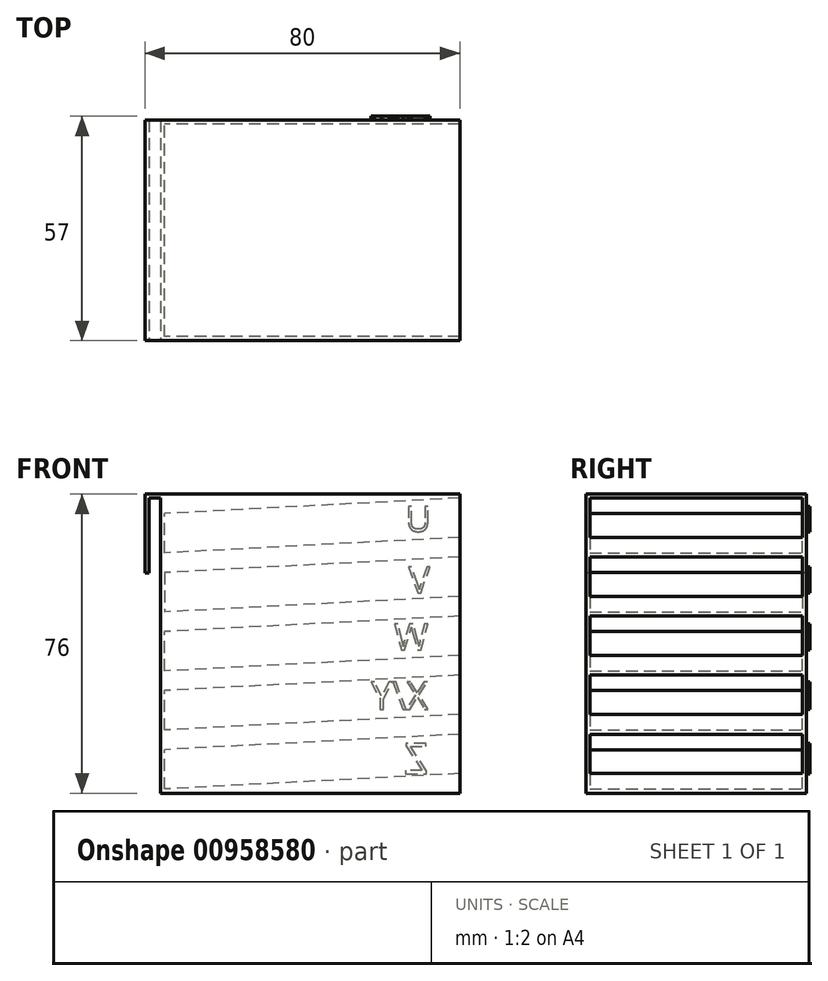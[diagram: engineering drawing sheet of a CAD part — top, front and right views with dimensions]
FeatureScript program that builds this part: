
annotation { "Feature Type Name" : "Feature", "Feature Type Description" : "" }
export const myFeature = defineFeature(function(context is Context, id is Id, definition is map)
    precondition{}
    {
        {
            var Q0;
            Q0=qCreatedBy(makeId("Front.planeOp"),FACE);
            var sketch = newSketch(context, id + "F0", { "sketchPlane" : qUnion([Q0])});
            skLineSegment(sketch, "E0.bottom", {"start": v(38, -38) * mm, "end": v(-38, -38) * mm});
            skLineSegment(sketch, "E0.top", {"start": v(38, 38) * mm, "end": v(-38, 38) * mm});
            skLineSegment(sketch, "E0.left", {"start": v(38, -38) * mm, "end": v(38, 38) * mm});
            skLineSegment(sketch, "E0.right", {"start": v(-38, -38) * mm, "end": v(-38, 38) * mm});
            skPoint(sketch, "E0.middle", {"position": v(0, 0) * mm});
            skSolve(sketch);
        }
        {
            var Q0;
            Q0=makeQuery(id+"F0.imprint","IMPRINT",FACE,{"disambiguationData":[TD([[makeQuery(id+"F0.imprint","IMPRINT",EDGE,{"derivedFrom":sQuery(id+"F0.wireOp",EDGE,"E0.bottom")}),-1.0]])]});
            extrude(context, id + "F1", {"entities" : qUnion([Q0]), "endBound" : BoundingType.SYMMETRIC, "oppositeDirection" : true, "depth" : 56 * mm, "offsetDistance" : 25 * mm});
        }
        {
            var Q0;
            Q0=makeQuery(id+"F1.opExtrude","SWEPT_FACE",FACE,{"disambiguationData":[OSD([sQuery(id+"F0.wireOp",EDGE,"E0.left")])]});
            var sketch = newSketch(context, id + "F2", { "sketchPlane" : qUnion([Q0])});
            skPoint(sketch, "E1", {"position": v(-28, 38) * mm});
            skPoint(sketch, "E2", {"position": v(-28, 37) * mm});
            skPoint(sketch, "E3", {"position": v(-27, 37) * mm});
            skLineSegment(sketch, "E4.bottom", {"start": v(-27, 37) * mm, "end": v(27, 37) * mm});
            skLineSegment(sketch, "E4.top", {"start": v(-27, 27) * mm, "end": v(27, 27) * mm});
            skLineSegment(sketch, "E4.left", {"start": v(-27, 37) * mm, "end": v(-27, 27) * mm});
            skLineSegment(sketch, "E4.right", {"start": v(27, 37) * mm, "end": v(27, 27) * mm});
            skPoint(sketch, "E5", {"position": v(-27, 27) * mm});
            skPoint(sketch, "E6", {"position": v(-27, 22) * mm});
            skLineSegment(sketch, "E7.bottom", {"start": v(-27, 22) * mm, "end": v(27, 22) * mm});
            skLineSegment(sketch, "E7.top", {"start": v(-27, 12) * mm, "end": v(27, 12) * mm});
            skLineSegment(sketch, "E7.left", {"start": v(-27, 22) * mm, "end": v(-27, 12) * mm});
            skLineSegment(sketch, "E7.right", {"start": v(27, 22) * mm, "end": v(27, 12) * mm});
            skPoint(sketch, "E8", {"position": v(-27, 7) * mm});
            skLineSegment(sketch, "E9.bottom", {"start": v(-27, 7) * mm, "end": v(27, 7) * mm});
            skLineSegment(sketch, "E9.top", {"start": v(-27, -3) * mm, "end": v(27, -3) * mm});
            skLineSegment(sketch, "E9.left", {"start": v(-27, 7) * mm, "end": v(-27, -3) * mm});
            skLineSegment(sketch, "E9.right", {"start": v(27, 7) * mm, "end": v(27, -3) * mm});
            skPoint(sketch, "E10", {"position": v(-27, -8) * mm});
            skLineSegment(sketch, "E11.bottom", {"start": v(-27, -8) * mm, "end": v(27, -8) * mm});
            skLineSegment(sketch, "E11.top", {"start": v(-27, -18) * mm, "end": v(27, -18) * mm});
            skLineSegment(sketch, "E11.left", {"start": v(-27, -8) * mm, "end": v(-27, -18) * mm});
            skLineSegment(sketch, "E11.right", {"start": v(27, -8) * mm, "end": v(27, -18) * mm});
            skPoint(sketch, "E12", {"position": v(-27, -23) * mm});
            skLineSegment(sketch, "E13.bottom", {"start": v(-27, -23) * mm, "end": v(27, -23) * mm});
            skLineSegment(sketch, "E13.top", {"start": v(-27, -33) * mm, "end": v(27, -33) * mm});
            skLineSegment(sketch, "E13.left", {"start": v(-27, -23) * mm, "end": v(-27, -33) * mm});
            skLineSegment(sketch, "E13.right", {"start": v(27, -23) * mm, "end": v(27, -33) * mm});
            skSolve(sketch);
        }
        {
            var Q0;
            Q0=makeQuery(id+"F1.opExtrude","CAP_FACE",FACE,{"disambiguationData":[OSD([sQuery(id+"F0.wireOp",EDGE,"E0.bottom"),sQuery(id+"F0.wireOp",EDGE,"E0.top"),sQuery(id+"F0.wireOp",EDGE,"E0.left"),sQuery(id+"F0.wireOp",EDGE,"E0.right")])],"isStart":true});
            var sketch = newSketch(context, id + "F3", { "sketchPlane" : qUnion([Q0])});
            skPoint(sketch, "E14", {"position": v(38, 22) * mm});
            skPoint(sketch, "E15", {"position": v(38, 7) * mm});
            skPoint(sketch, "E16", {"position": v(38, -8) * mm});
            skPoint(sketch, "E17", {"position": v(38, -23) * mm});
            skPoint(sketch, "E18", {"position": v(38, 37) * mm});
            skLineSegment(sketch, "E19", {"start": v(-38, 33.02) * mm, "end": v(-10.2, 33.02) * mm, "construction": true});
            skLineSegment(sketch, "E20", {"start": v(38, 37) * mm, "end": v(-38, 33.02) * mm});
            skLineSegment(sketch, "E21", {"start": v(38, 22) * mm, "end": v(-38, 18.02) * mm});
            skLineSegment(sketch, "E22", {"start": v(-38, 18.02) * mm, "end": v(-8.95, 18.02) * mm, "construction": true});
            skLineSegment(sketch, "E23", {"start": v(38, -23) * mm, "end": v(-38, -26.98) * mm});
            skLineSegment(sketch, "E24", {"start": v(-38, -26.98) * mm, "end": v(-9.06, -26.98) * mm, "construction": true});
            skLineSegment(sketch, "E25", {"start": v(38, 7) * mm, "end": v(-38, 3.02) * mm});
            skLineSegment(sketch, "E26", {"start": v(-38, 3.02) * mm, "end": v(-5.53, 3.02) * mm, "construction": true});
            skLineSegment(sketch, "E27", {"start": v(38, -8) * mm, "end": v(-38, -11.98) * mm});
            skLineSegment(sketch, "E28", {"start": v(-38, -11.98) * mm, "end": v(-6.01, -11.98) * mm});
            skSolve(sketch);
        }
        {
            var Q0;
            Q0=makeQuery(id+"F2.imprint","IMPRINT",FACE,{"disambiguationData":[TD([[makeQuery(id+"F2.imprint","IMPRINT",EDGE,{"derivedFrom":sQuery(id+"F2.wireOp",EDGE,"E4.bottom")}),-1.0]])]});
            var Q1;
            Q1=makeQuery(id+"F2.imprint","IMPRINT",FACE,{"disambiguationData":[TD([[makeQuery(id+"F2.imprint","IMPRINT",EDGE,{"derivedFrom":sQuery(id+"F2.wireOp",EDGE,"E7.bottom")}),-1.0]])]});
            var Q2;
            Q2=makeQuery(id+"F2.imprint","IMPRINT",FACE,{"disambiguationData":[TD([[makeQuery(id+"F2.imprint","IMPRINT",EDGE,{"derivedFrom":sQuery(id+"F2.wireOp",EDGE,"E9.bottom")}),-1.0]])]});
            var Q3;
            Q3=makeQuery(id+"F2.imprint","IMPRINT",FACE,{"disambiguationData":[TD([[makeQuery(id+"F2.imprint","IMPRINT",EDGE,{"derivedFrom":sQuery(id+"F2.wireOp",EDGE,"E11.bottom")}),-1.0]])]});
            var Q4;
            Q4=makeQuery(id+"F2.imprint","IMPRINT",FACE,{"disambiguationData":[TD([[makeQuery(id+"F2.imprint","IMPRINT",EDGE,{"derivedFrom":sQuery(id+"F2.wireOp",EDGE,"E13.bottom")}),-1.0]])]});
            var Q5;
            Q5=sQuery(id+"F3.wireOp",EDGE,"E20");
            sweep(context, id + "F4", {"operationType" : NewBodyOperationType.REMOVE, "profiles" : qUnion([Q0, Q1, Q2, Q3, Q4]), "path" : qUnion([Q5])});
        }
        {
            var Q0;
            Q0=makeQuery(id+"F1.opExtrude","SWEPT_FACE",FACE,{"disambiguationData":[OSD([sQuery(id+"F0.wireOp",EDGE,"E0.right")])]});
            var sketch = newSketch(context, id + "F5", { "sketchPlane" : qUnion([Q0])});
            skLineSegment(sketch, "E29.bottom", {"start": v(-28, 38) * mm, "end": v(28, 38) * mm});
            skLineSegment(sketch, "E29.top", {"start": v(-28, -38) * mm, "end": v(28, -38) * mm});
            skLineSegment(sketch, "E29.left", {"start": v(-28, 38) * mm, "end": v(-28, -38) * mm});
            skLineSegment(sketch, "E29.right", {"start": v(28, 38) * mm, "end": v(28, -38) * mm});
            skSolve(sketch);
        }
        {
            var Q0;
            Q0=qSketchRegion(id+"F5",true);
            extrude(context, id + "F6", {"entities" : qUnion([Q0]), "operationType" : NewBodyOperationType.ADD, "oppositeDirection" : true, "depth" : 1 * mm, "offsetDistance" : 25 * mm});
        }
        {
            var Q0;
            Q0=makeQuery(id+"F1.opExtrude","CAP_FACE",FACE,{"disambiguationData":[OSD([sQuery(id+"F0.wireOp",EDGE,"E0.bottom"),sQuery(id+"F0.wireOp",EDGE,"E0.top"),sQuery(id+"F0.wireOp",EDGE,"E0.left"),sQuery(id+"F0.wireOp",EDGE,"E0.right")])],"isStart":true});
            var sketch = newSketch(context, id + "F7", { "sketchPlane" : qUnion([Q0])});
            skLineSegment(sketch, "E30", {"start": v(-38, 38) * mm, "end": v(-42, 38) * mm});
            skLineSegment(sketch, "E31", {"start": v(-42, 38) * mm, "end": v(-42, 18) * mm});
            skLineSegment(sketch, "E32", {"start": v(-42, 18) * mm, "end": v(-41, 18) * mm});
            skLineSegment(sketch, "E33", {"start": v(-41, 18) * mm, "end": v(-41, 37) * mm});
            skLineSegment(sketch, "E34", {"start": v(-41, 37) * mm, "end": v(-38, 37) * mm});
            skSolve(sketch);
        }
        {
            var Q0;
            {var subQ0=sQuery(id+"F7.wireOp",EDGE,"E30");Q0=makeQuery(id+"F7.imprint","IMPRINT",FACE,{"disambiguationData":[TD([[makeQuery(id+"F7.imprint","IMPRINT",EDGE,{"derivedFrom":subQ0}),1.0]])]});}
            extrude(context, id + "F8", {"entities" : qUnion([Q0]), "operationType" : NewBodyOperationType.ADD, "oppositeDirection" : true, "depth" : 56 * mm, "offsetDistance" : 25 * mm});
        }
        {
            var Q0;
            {var subQ0=sQuery(id+"F0.wireOp",EDGE,"E0.right");Q0=makeQuery(id+"F8.boolean.opBoolean","MERGE",FACE,{"derivedFrom":[makeQuery(id+"F1.opExtrude","CAP_FACE",FACE,{"disambiguationData":[OSD([sQuery(id+"F0.wireOp",EDGE,"E0.bottom"),sQuery(id+"F0.wireOp",EDGE,"E0.top"),sQuery(id+"F0.wireOp",EDGE,"E0.left"),subQ0])],"isStart":false}),makeQuery(id+"F8.opExtrude","CAP_FACE",FACE,{"disambiguationData":[OSD([subQ0,sQuery(id+"F7.wireOp",EDGE,"E30"),sQuery(id+"F7.wireOp",EDGE,"E31"),sQuery(id+"F7.wireOp",EDGE,"E32"),sQuery(id+"F7.wireOp",EDGE,"E33"),sQuery(id+"F7.wireOp",EDGE,"E34")])],"isStart":false})]});}
            var sketch = newSketch(context, id + "F9", { "sketchPlane" : qUnion([Q0])});
            skText(sketch, "E35", { "text": "U", "fontName": "OpenSans-Regular.ttf"});
            skText(sketch, "E36", { "text": "V", "fontName": "OpenSans-Regular.ttf"});
            skText(sketch, "E37", { "text": "W", "fontName": "OpenSans-Regular.ttf"});
            skText(sketch, "E38", { "text": "X/Y", "fontName": "OpenSans-Regular.ttf"});
            skText(sketch, "E39", { "text": "Z", "fontName": "OpenSans-Regular.ttf"});
            const initialGuessF9  = {"E35": [-0.03067, 0.02852, 1, 0, 0.00643], "E36": [-0.03044, 0.01292, 1, 0, 0.00667], "E37": [-0.02997, -0.00164, 1, 0, 0.00676], "E38": [-0.02997, -0.01666, 1, 0, 0.00695], "E39": [-0.02997, -0.03303, 1, 0, 0.0078]};
            skSetInitialGuess(sketch, initialGuessF9);
            skSolve(sketch);
        }
        {
            var Q0;
            Q0=qSketchRegion(id+"F9",true);
            extrude(context, id + "F10", {"entities" : qUnion([Q0]), "operationType" : NewBodyOperationType.ADD, "depth" : 1 * mm, "offsetDistance" : 25 * mm});
        }
    });
